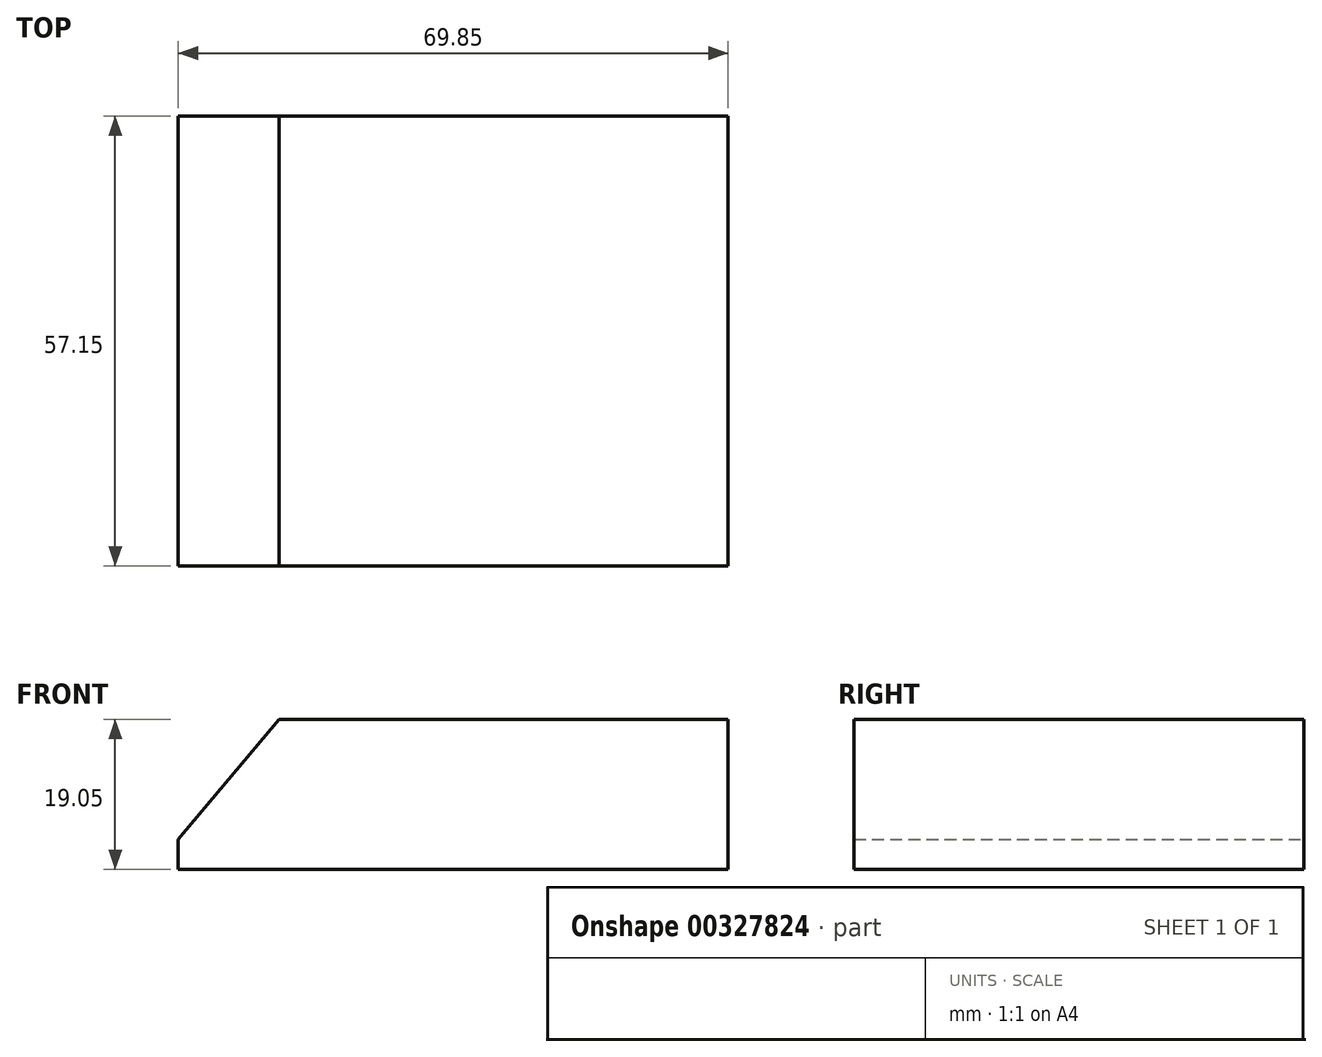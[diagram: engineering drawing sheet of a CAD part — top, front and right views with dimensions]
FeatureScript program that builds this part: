
annotation { "Feature Type Name" : "Feature", "Feature Type Description" : "" }
export const myFeature = defineFeature(function(context is Context, id is Id, definition is map)
    precondition{}
    {
        {
            var Q0;
            Q0=qCreatedBy(makeId("Front.planeOp"),FACE);
            var sketch = newSketch(context, id + "F0", { "sketchPlane" : qUnion([Q0])});
            skLineSegment(sketch, "E0.bottom", {"start": v(0, 0) * mm, "end": v(69.85, 0) * mm});
            skLineSegment(sketch, "E0.top", {"start": v(0, 19.05) * mm, "end": v(69.85, 19.05) * mm});
            skLineSegment(sketch, "E0.left", {"start": v(0, 0) * mm, "end": v(0, 19.05) * mm});
            skLineSegment(sketch, "E0.right", {"start": v(69.85, 0) * mm, "end": v(69.85, 19.05) * mm});
            skSolve(sketch);
        }
        {
            var Q0;
            Q0 = qSketchRegion(id + "F0", true);
            extrude(context, id + "F1", {"entities" : qUnion([Q0]), "depth" : 57.15 * mm});
        }
        {
            var Q0;
            Q0=makeQuery(id+"F1.opExtrude","SWEPT_EDGE",EDGE,{"disambiguationData":[OSD([sQuery(id+"F0.wireOp",EDGE,"E0.top"),sQuery(id+"F0.wireOp",EDGE,"E0.left")])]});
            chamfer(context, id + "F2", {"entities" : qUnion([Q0]), "chamferType" : ChamferType.OFFSET_ANGLE, "width" : 15.24 * mm, "oppositeDirection" : false, "angle" : 40 * degree, "tangentPropagation" : true});
        }
    });
